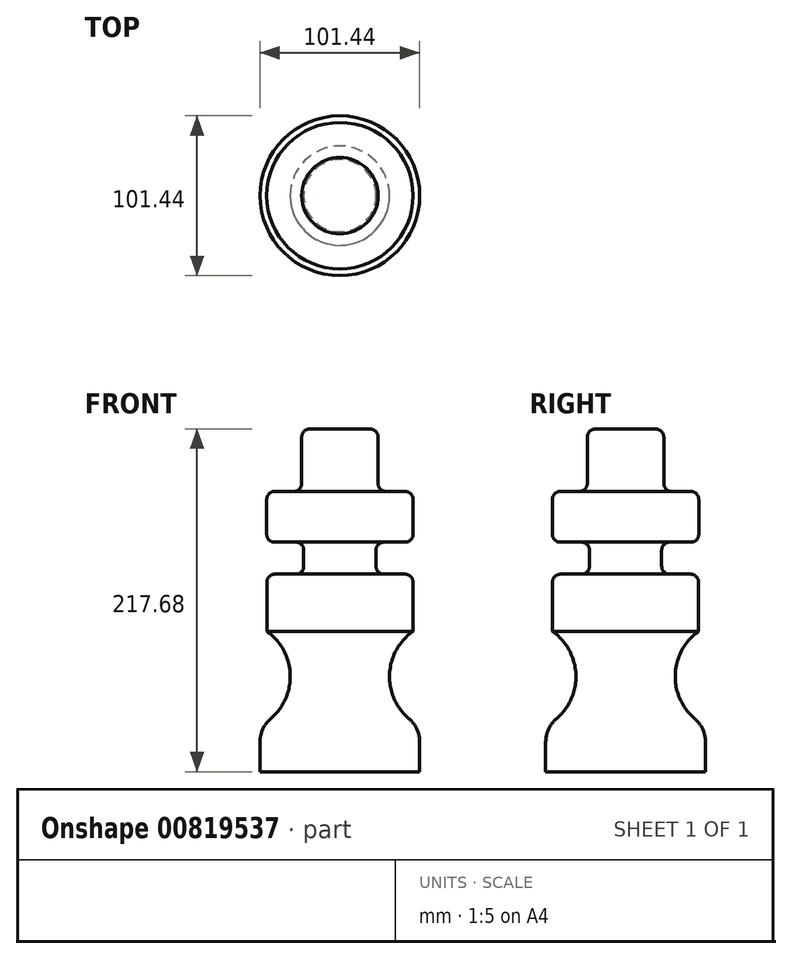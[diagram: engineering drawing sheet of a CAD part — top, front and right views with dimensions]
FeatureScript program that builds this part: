
annotation { "Feature Type Name" : "Feature", "Feature Type Description" : "" }
export const myFeature = defineFeature(function(context is Context, id is Id, definition is map)
    precondition{}
    {
        {
            var Q0;
            Q0=qCreatedBy(makeId("Top.planeOp"),FACE);
            var sketch = newSketch(context, id + "F0", { "sketchPlane" : qUnion([Q0])});
            skCircle(sketch, "E0", {"center": v(0, 0) * mm, "radius": 50.72 * mm});
            skSolve(sketch);
        }
        {
            var Q0;
            Q0 = qSketchRegion(id + "F0", true);
            extrude(context, id + "F1", {"entities" : qUnion([Q0]), "depth" : 38.1 * mm, "offsetDistance" : 25.4 * mm});
        }
        {
            var Q0;
            Q0=qCreatedBy(makeId("Top.planeOp"),FACE);
            var sketch = newSketch(context, id + "F2", { "sketchPlane" : qUnion([Q0])});
            skCircle(sketch, "E1", {"center": v(0, 0) * mm, "radius": 31.54 * mm});
            skSolve(sketch);
        }
        {
            var Q0;
            Q0 = qSketchRegion(id + "F2", true);
            extrude(context, id + "F3", {"entities" : qUnion([Q0]), "operationType" : NewBodyOperationType.ADD, "depth" : 90.17 * mm, "offsetDistance" : 25.4 * mm});
        }
        {
            var Q0;
            Q0=qCreatedBy(makeId("Top.planeOp"),FACE);
            var sketch = newSketch(context, id + "F4", { "sketchPlane" : qUnion([Q0])});
            skCircle(sketch, "E2", {"center": v(0, 0) * mm, "radius": 46.4 * mm});
            skSolve(sketch);
        }
        {
            var Q0;
            Q0 = qSketchRegion(id + "F4", true);
            extrude(context, id + "F5", {"entities" : qUnion([Q0]), "operationType" : NewBodyOperationType.ADD, "depth" : 125.48 * mm, "offsetDistance" : 25.4 * mm, "hasSecondDirection" : true, "secondDirectionOppositeDirection" : false, "secondDirectionDepth" : 89.15 * mm});
        }
        {
            var Q0;
            Q0=qCreatedBy(makeId("Top.planeOp"),FACE);
            var sketch = newSketch(context, id + "F6", { "sketchPlane" : qUnion([Q0])});
            skCircle(sketch, "E3", {"center": v(0, 0) * mm, "radius": 22.94 * mm});
            skSolve(sketch);
        }
        {
            var Q0;
            Q0 = qSketchRegion(id + "F6", true);
            extrude(context, id + "F7", {"entities" : qUnion([Q0]), "operationType" : NewBodyOperationType.ADD, "depth" : 150.88 * mm, "offsetDistance" : 25.4 * mm, "hasSecondDirection" : true, "secondDirectionOppositeDirection" : false, "secondDirectionDepth" : 121.16 * mm});
        }
        {
            var Q0;
            Q0=qCreatedBy(makeId("Top.planeOp"),FACE);
            var sketch = newSketch(context, id + "F8", { "sketchPlane" : qUnion([Q0])});
            skCircle(sketch, "E4", {"center": v(0, 0) * mm, "radius": 46.48 * mm});
            skSolve(sketch);
        }
        {
            var Q0;
            Q0 = qSketchRegion(id + "F8", true);
            extrude(context, id + "F9", {"entities" : qUnion([Q0]), "operationType" : NewBodyOperationType.ADD, "depth" : 178.05 * mm, "offsetDistance" : 25.4 * mm, "hasSecondDirection" : true, "secondDirectionOppositeDirection" : false, "secondDirectionDepth" : 145.8 * mm});
        }
        {
            var Q0;
            Q0=qCreatedBy(makeId("Top.planeOp"),FACE);
            var sketch = newSketch(context, id + "F10", { "sketchPlane" : qUnion([Q0])});
            skCircle(sketch, "E5", {"center": v(0, 0) * mm, "radius": 24.26 * mm});
            skSolve(sketch);
        }
        {
            var Q0;
            Q0 = qSketchRegion(id + "F10", true);
            extrude(context, id + "F11", {"entities" : qUnion([Q0]), "operationType" : NewBodyOperationType.ADD, "depth" : 217.68 * mm, "offsetDistance" : 25.4 * mm, "hasSecondDirection" : true, "secondDirectionOppositeDirection" : false, "secondDirectionDepth" : 176.53 * mm});
        }
        {
            var Q0;
            Q0=makeQuery(id+"F1.opExtrude","CAP_EDGE",EDGE,{"disambiguationData":[OSD([sQuery(id+"F0.wireOp",EDGE,"E0")])],"isStart":false});
            fillet(context, id + "F12", {"entities" : qUnion([Q0]), "radius" : 19.05 * mm, "tangentPropagation" : true, "allowEdgeOverflow" : false});
        }
        {
            var Q0;
            Q0=makeQuery(id+"F3.opExtrude","SWEPT_FACE",FACE,{"disambiguationData":[OSD([sQuery(id+"F2.wireOp",EDGE,"E1")])]});
            fillet(context, id + "F13", {"entities" : qUnion([Q0]), "radius" : 35.18 * mm, "tangentPropagation" : true, "allowEdgeOverflow" : false});
        }
        {
            var Q0;
            Q0=makeQuery(id+"F5.opExtrude","CAP_EDGE",EDGE,{"disambiguationData":[OSD([sQuery(id+"F4.wireOp",EDGE,"E2")])],"isStart":false});
            fillet(context, id + "F14", {"entities" : qUnion([Q0]), "radius" : 5.08 * mm, "tangentPropagation" : true, "allowEdgeOverflow" : false});
        }
        {
            var Q0;
            Q0=makeQuery(id+"F7.opExtrude","SWEPT_FACE",FACE,{"disambiguationData":[OSD([sQuery(id+"F6.wireOp",EDGE,"E3")])]});
            fillet(context, id + "F15", {"entities" : qUnion([Q0]), "radius" : 5.08 * mm, "tangentPropagation" : true, "allowEdgeOverflow" : false});
        }
        {
            var Q0;
            Q0=makeQuery(id+"F9.opExtrude","CAP_EDGE",EDGE,{"disambiguationData":[OSD([sQuery(id+"F8.wireOp",EDGE,"E4")])],"isStart":true});
            var Q1;
            Q1=makeQuery(id+"F9.opExtrude","CAP_EDGE",EDGE,{"disambiguationData":[OSD([sQuery(id+"F8.wireOp",EDGE,"E4")])],"isStart":false});
            var Q2;
            Q2=makeQuery(id+"F11.boolean.opBoolean","INTERSECT",EDGE,{"derivedFrom":[makeQuery(id+"F9.opExtrude","CAP_FACE",FACE,{"disambiguationData":[OSD([sQuery(id+"F8.wireOp",EDGE,"E4")])],"isStart":false}),makeQuery(id+"F11.opExtrude","SWEPT_FACE",FACE,{"disambiguationData":[OSD([sQuery(id+"F10.wireOp",EDGE,"E5")])]})]});
            var Q3;
            Q3=makeQuery(id+"F11.opExtrude","SWEPT_FACE",FACE,{"disambiguationData":[OSD([sQuery(id+"F10.wireOp",EDGE,"E5")])]});
            fillet(context, id + "F16", {"entities" : qUnion([Q0, Q1, Q2, Q3]), "radius" : 5.08 * mm, "tangentPropagation" : true, "allowEdgeOverflow" : false});
        }
    });
